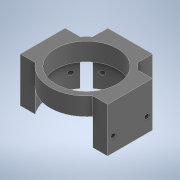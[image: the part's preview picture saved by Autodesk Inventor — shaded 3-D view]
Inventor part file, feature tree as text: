
AUTODESK INVENTOR PART (.ipt)
format: ipt  version: 2022 (Build 260153000, 153)  size: 252,416 bytes
history: native  units: mm
features: sketch x11, extrude x9, plane x1
ambient origin geometry x8: Origin, YZ Plane, XZ Plane, XY Plane, X Axis, Y Axis, Z Axis, Center Point
bodies: Solid1 (feature_tree)
feature tree (21):
  sketch  "Sketch1"  dims[d0=27.5mm d1=43.0mm]
  sketch  "Sketch2"  dims[d2=43.0mm d3=21.5mm]
  extrude  "Extrusion1"  Depth=43.0mm
  extrude  "Extrusion2"  Depth=21.5mm
  extrude  "Extrusion3"  Depth=32.5mm
  extrude  "Extrusion4"  Depth=8.0mm
  plane  "Work Plane1"
  extrude  "Extrusion7"  Depth=16.5mm
  extrude  "Extrusion8"  Depth=16.5mm
  extrude  "Extrusion9"  Depth=16.5mm
  extrude  "Extrusion5"  Depth=33.0mm
  extrude  "Extrusion6"  Depth=10.0mm
  sketch  "Sketch8"  dims[d15=15.0mm d16=33.0mm]
  sketch  "Sketch3"  dims[d4=21.5mm d5=32.5mm]
  sketch  "Sketch4"  dims[d6=8.0mm d7=0.0mm d8=33.0mm]
  sketch  "Sketch5"  dims[d9=15.0mm d10=16.5mm]
  sketch  "Sketch6"  dims[d11=15.0mm d12=16.5mm]
  sketch  "Sketch7"  dims[d13=33.0mm d14=16.5mm]
  sketch  "Sketch9"  dims[d18=10.0mm d19=20.0mm d20=10.0mm]
  sketch  "Sketch10"  dims[d21=10.0mm]
  sketch  "Sketch11"  dims[d22=20.0mm d23=0.0mm d26=33.0mm d27=20.0mm d28=16.5mm d29=7.5mm d30=7.5mm d31=5.5mm d32=2.0mm d33=2.0mm d34=0.0mm d35=0.0mm d36=5.5mm d37=2.0mm d38=2.0mm d39=7.5mm d40=7.5mm d41=0.0mm d42=0.0mm d43=16.25mm d44=21.0mm d45=10.5mm d46=31.0mm d47=2.0mm d48=2.0mm d49=4.8mm d50=4.8mm d51=2.0mm d52=2.0mm d53=10.0mm d54=0.0mm d55=3.0mm d56=0.0mm d57=3.0mm d58=0.0mm d59=3.0mm d60=0.0mm d61=3.0mm d62=0.0mm]
